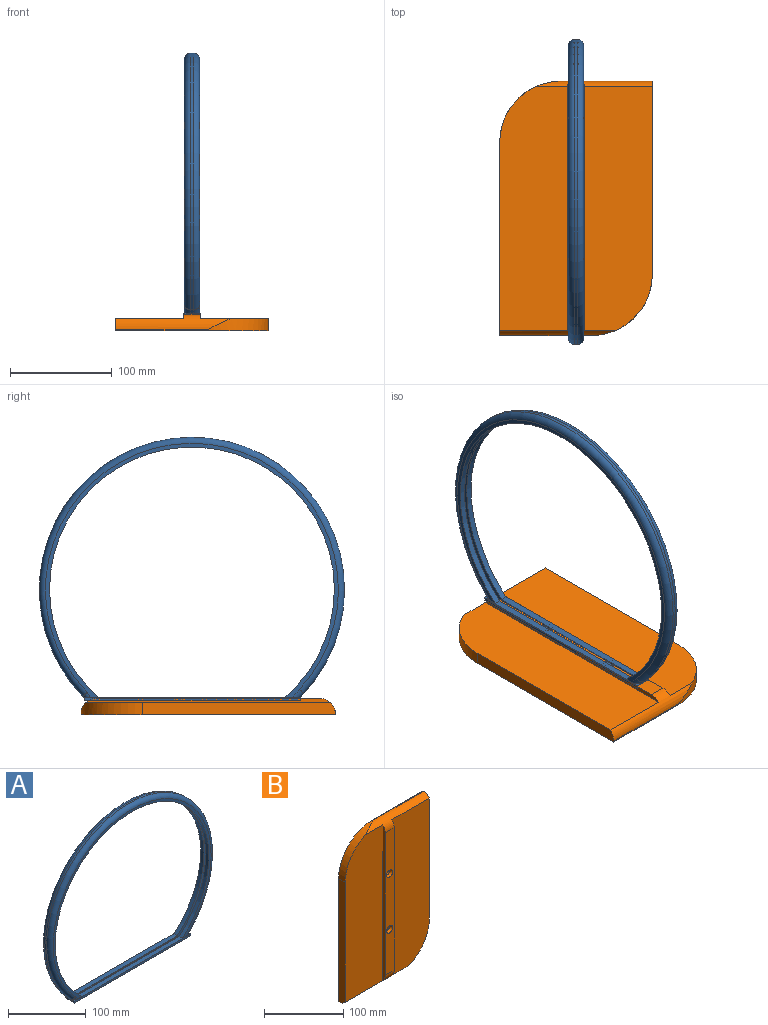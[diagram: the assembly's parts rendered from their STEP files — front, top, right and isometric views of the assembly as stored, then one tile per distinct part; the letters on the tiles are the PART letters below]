
ASSEMBLY  parts=2 mates=1
PART A: 35 faces, bbox 325.1x17.3x276.9 mm
  f0: plane 212x6.5mm, normal (0,0,1), area 1217.2mm2, adj f1,f5,f7,f8,f9,f12,f29,f32
  f1: cylinder r=140mm len=280mm, axis (0,-1,0), area 4083.9mm2, adj f0,f5,f12
  f2: plane 212.4x6.9mm, normal (0,0,1), area 1217.2mm2, adj f4,f6,f7,f9,f10,f13,f25,f28
  f3: cylinder r=150mm len=300mm, axis (0,1,0), area 2098mm2, adj f16,f17,f18,f20,f26,f30
  f4: plane 288x249.8mm, normal (0,-1,0), area 2689.5mm2, adj f2,f6,f25,f26,f28
  f5: plane 288x249.8mm, normal (0,1,0), area 2689.5mm2, adj f0,f1,f29,f30,f32
  f6: cylinder r=140mm len=280mm, axis (0,-1,0), area 4083.9mm2, adj f2,f4,f13
  f7: plane 16x3mm, normal (1,0,0), area 48mm2, adj f0,f2,f8,f10,f11,f20
  f8: plane 212x3mm, normal (0,1,0), area 636mm2, adj f0,f7,f9,f11
  f9: plane 16.13x3.13mm, normal (-1,0,0), area 30.3mm2, adj f0,f2,f8,f10,f11,f19,f28,f32
  f10: plane 212x3mm, normal (0,-1,0), area 636mm2, adj f2,f7,f9,f11
  f11: plane 212x16mm, normal (0,0,-1), area 3195mm2, adj f7,f8,f9,f10,f33,f34
  f12: plane 290x252.68mm, normal (0,-1,0), area 3742.5mm2, adj f0,f1,f14,f15
  f13: plane 290x252.68mm, normal (0,1,0), area 3742.5mm2, adj f2,f6,f14,f15
  f14: cylinder r=145mm len=290mm, axis (0,-1,0), area 2089.2mm2, adj f12,f13,f15,f16
  f15: plane 194.23x3mm, normal (0,0,1), area 582.7mm2, adj f12,f13,f14
  f16: cylinder r=1mm len=9.57mm, axis (1,0,0), area 48.2mm2, adj f3,f14,f17,f18,f19
  f17: cylinder r=3.5mm len=1.38mm, axis (0,-1,0), area 0.3mm2, adj f3,f16,f19,f31
  f18: cylinder r=3.5mm len=1.38mm, axis (0,-1,0), area 0.3mm2, adj f3,f16,f19,f27
  f19: cylinder r=5mm len=3.73mm, axis (0,-1,0), area 8.9mm2, adj f9,f16,f17,f18,f28,f32
  f20: cylinder r=228mm len=3.89mm, axis (0,-1,0), area 15.8mm2, adj f3,f7,f25,f29
  f21: cylinder r=2.5mm len=5mm, axis (0,0,1), area 29.8mm2, adj f22,f34
  f22: plane 5x5mm, normal (0,0,-1), area 19.6mm2, adj f21
  f23: cylinder r=2.5mm len=5mm, axis (0,0,1), area 29.8mm2, adj f24,f33
  f24: plane 5x5mm, normal (0,0,-1), area 19.6mm2, adj f23
  f25: torus R=234mm, axis (0,-1,0), area 68mm2, adj f2,f4,f20,f26
  f26: torus R=144mm, axis (0,-1,0), area 6494.8mm2, adj f3,f4,f25,f27
  f27: bspline ~7.34x4.42mm, area 0.9mm2, adj f18,f26,f28
  f28: torus R=11mm, axis (0,-1,0), area 32.7mm2, adj f2,f4,f9,f19,f27
  f29: torus R=234mm, axis (0,-1,0), area 68mm2, adj f0,f5,f20,f30
  f30: torus R=144mm, axis (0,-1,0), area 6494.8mm2, adj f3,f5,f29,f31
  f31: bspline ~7.34x4.42mm, area 0.9mm2, adj f17,f30,f32
  f32: torus R=11mm, axis (0,-1,0), area 33.5mm2, adj f0,f5,f9,f19,f31
  f33: torus R=5.6mm, axis (0,0,1), area 111mm2, adj f11,f23
  f34: torus R=5.6mm, axis (0,0,1), area 111mm2, adj f11,f21
PART B: 20 faces, bbox 150x16x250 mm
  f0: plane 240.4x67mm, normal (0,-1,0), area 15546.2mm2, adj f2,f3,f9,f12,f13
  f1: plane 90x1mm, normal (0,0,-1), area 90mm2, adj f2,f6,f8,f13
  f2: cylinder r=60mm len=60mm, axis (0,1,0), area 1004.6mm2, adj f0,f1,f3,f8,f13
  f3: plane 190x12mm, normal (1,0,0), area 2263.7mm2, adj f0,f2,f4,f8,f12
  f4: plane 90x1mm, normal (0,0,1), area 90mm2, adj f3,f5,f8,f12
  f5: cylinder r=60mm len=60mm, axis (0,1,0), area 1004.6mm2, adj f4,f6,f7,f8,f12
  f6: plane 190x12mm, normal (-1,0,0), area 2263.7mm2, adj f1,f5,f7,f8,f13
  f7: plane 240.4x67mm, normal (0,-1,0), area 15546.2mm2, adj f5,f6,f10,f12,f13
  f8: plane 250x150mm, normal (0,1,0), area 35954.9mm2, adj f1,f2,f3,f4,f5,f6
  f9: plane 240.4x4mm, normal (1,0,0), area 936mm2, adj f0,f11,f12,f13
  f10: plane 240.4x4mm, normal (-1,0,0), area 936mm2, adj f7,f11,f12,f13
  f11: plane 220x16mm, normal (0,-1,0), area 3329.9mm2, adj f9,f10,f12,f13,f18,f19
  f12: cylinder r=15mm len=113.52mm, axis (1,0,0), area 1439.6mm2, adj f0,f3,f4,f5,f7,f9,f10,f11
  f13: cylinder r=15mm len=113.52mm, axis (-1,0,0), area 1439.6mm2, adj f0,f1,f2,f6,f7,f9,f10,f11
  f14: cylinder r=2.5mm len=5mm, axis (0,-1,0), area 62.8mm2, adj f15,f19
  f15: plane 5x5mm, normal (0,-1,0), area 19.6mm2, adj f14
  f16: cylinder r=2.5mm len=5mm, axis (0,-1,0), area 62.8mm2, adj f17,f18
  f17: plane 5x5mm, normal (0,-1,0), area 19.6mm2, adj f16
  f18: cone r=2.5mm half-angle=45deg, axis (0,-1,0), area 106.6mm2, adj f11,f16
  f19: cone r=2.5mm half-angle=45deg, axis (0,-1,0), area 106.6mm2, adj f11,f14
PLACE A rot(axis=(0,0,-1),90deg) t=(294.49,-16.1,-58.79)mm
PLACE B rot(axis=(-1,0,0),90deg) t=(294.49,-16.54,-75.79)mm
MATE fastened A.f21 <-> B.f16  axis (0,0,-1) through (294.49,11.46,-66.79)mm
